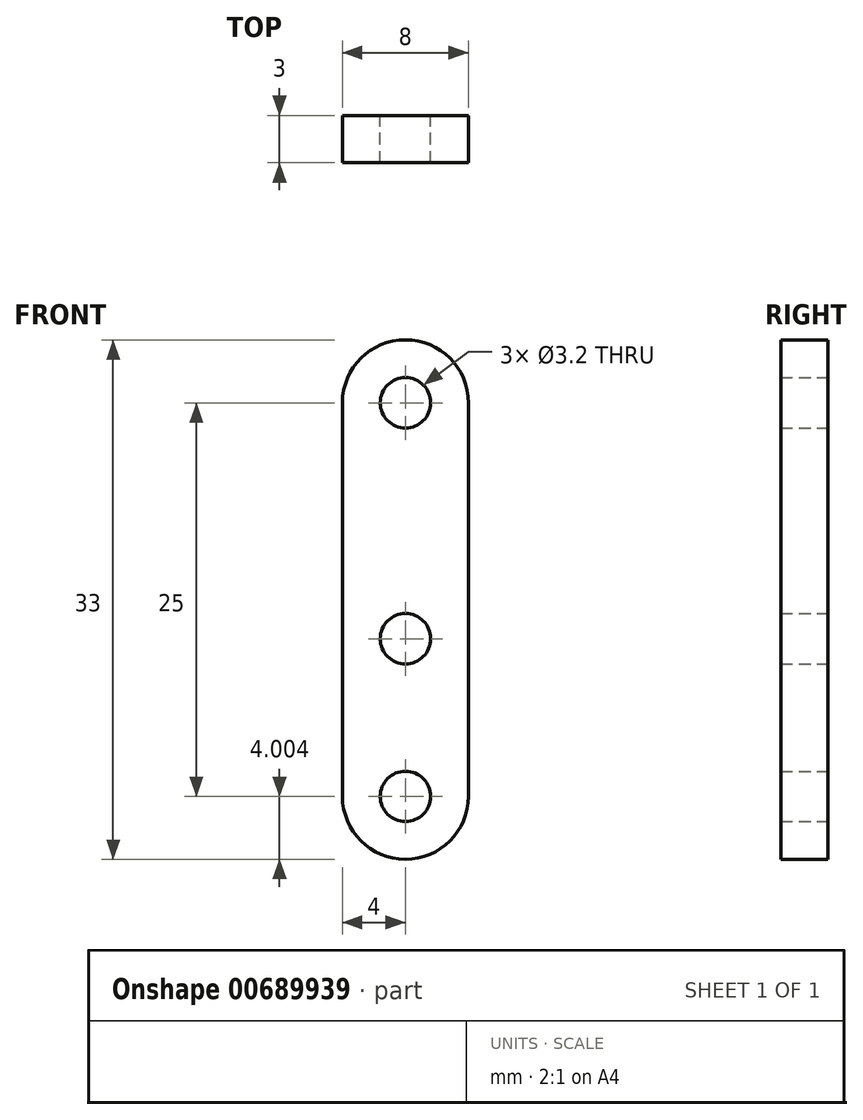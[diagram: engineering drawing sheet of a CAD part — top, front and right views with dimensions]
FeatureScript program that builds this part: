
annotation { "Feature Type Name" : "Feature", "Feature Type Description" : "" }
export const myFeature = defineFeature(function(context is Context, id is Id, definition is map)
    precondition{}
    {
        {
            var Q0;
            Q0=qCreatedBy(makeId("Front.planeOp"),FACE);
            var sketch = newSketch(context, id + "F0", { "sketchPlane" : qUnion([Q0])});
            skLineSegment(sketch, "E0.bottom", {"start": v(4, 5.91) * mm, "end": v(-4, 5.91) * mm});
            skLineSegment(sketch, "E0.top", {"start": v(4, -19.09) * mm, "end": v(-4, -19.09) * mm});
            skLineSegment(sketch, "E0.left", {"start": v(4, 5.91) * mm, "end": v(4, -19.09) * mm});
            skLineSegment(sketch, "E0.right", {"start": v(-4, 5.91) * mm, "end": v(-4, -19.09) * mm});
            skPoint(sketch, "E0.middle", {"position": v(0, -6.59) * mm});
            skCircle(sketch, "E1", {"center": v(0, 5.91) * mm, "radius": 1.6 * mm});
            skCircle(sketch, "E2", {"center": v(0, -19.09) * mm, "radius": 1.6 * mm});
            skCircle(sketch, "E3.0", {"center": v(0, 5.91) * mm, "radius": 4 * mm});
            skCircle(sketch, "E4.0", {"center": v(0, -19.09) * mm, "radius": 4 * mm});
            skCircle(sketch, "E5", {"center": v(0, -9.07) * mm, "radius": 1.6 * mm});
            skSolve(sketch);
        }
        {
            var Q0;
            {var subQ0=sQuery(id+"F0.wireOp",EDGE,"E3.0");var subQ1=sQuery(id+"F0.wireOp",EDGE,"E0.left");var subQ2=makeQuery(id+"F0.imprint","INTERSECT",VERTEX,{"derivedFrom":[subQ1,subQ0]});Q0=makeQuery(id+"F0.imprint","IMPRINT",FACE,{"disambiguationData":[TD([[makeQuery(id+"F0.imprint","IMPRINT",EDGE,{"disambiguationData":[TD([[subQ2,-1.0]])],"derivedFrom":subQ1}),-1.0]])]});}
            var Q1;
            {var subQ1=sQuery(id+"F0.wireOp",EDGE,"E0.bottom");var subQ5=sQuery(id+"F0.wireOp",EDGE,"E0.left");var subQ6=makeQuery(id+"F0.imprint","INTERSECT",VERTEX,{"derivedFrom":[subQ1,subQ5]});Q1=makeQuery(id+"F0.imprint","IMPRINT",FACE,{"disambiguationData":[TD([[makeQuery(id+"F0.imprint","IMPRINT",EDGE,{"disambiguationData":[TD([[subQ6,-1.0]])],"derivedFrom":subQ1}),-1.0]])]});}
            var Q2;
            {var subQ1=sQuery(id+"F0.wireOp",EDGE,"E0.top");var subQ7=sQuery(id+"F0.wireOp",EDGE,"E0.left");var subQ8=makeQuery(id+"F0.imprint","INTERSECT",VERTEX,{"derivedFrom":[subQ1,subQ7]});Q2=makeQuery(id+"F0.imprint","IMPRINT",FACE,{"disambiguationData":[TD([[makeQuery(id+"F0.imprint","IMPRINT",EDGE,{"disambiguationData":[TD([[subQ8,-1.0]])],"derivedFrom":subQ1}),1.0]])]});}
            var Q3;
            {var subQ1=sQuery(id+"F0.wireOp",EDGE,"E0.top");var subQ7=sQuery(id+"F0.wireOp",EDGE,"E0.left");var subQ8=makeQuery(id+"F0.imprint","INTERSECT",VERTEX,{"derivedFrom":[subQ1,subQ7]});Q3=makeQuery(id+"F0.imprint","IMPRINT",FACE,{"disambiguationData":[TD([[makeQuery(id+"F0.imprint","IMPRINT",EDGE,{"disambiguationData":[TD([[subQ8,-1.0]])],"derivedFrom":subQ1}),-1.0]])]});}
            var Q4;
            {var subQ1=sQuery(id+"F0.wireOp",EDGE,"E0.bottom");var subQ5=sQuery(id+"F0.wireOp",EDGE,"E0.left");var subQ6=makeQuery(id+"F0.imprint","INTERSECT",VERTEX,{"derivedFrom":[subQ1,subQ5]});Q4=makeQuery(id+"F0.imprint","IMPRINT",FACE,{"disambiguationData":[TD([[makeQuery(id+"F0.imprint","IMPRINT",EDGE,{"disambiguationData":[TD([[subQ6,-1.0]])],"derivedFrom":subQ1}),1.0]])]});}
            extrude(context, id + "F1", {"entities" : qUnion([Q0, Q1, Q2, Q3, Q4]), "depth" : 3 * mm, "offsetDistance" : 25 * mm});
        }
    });
